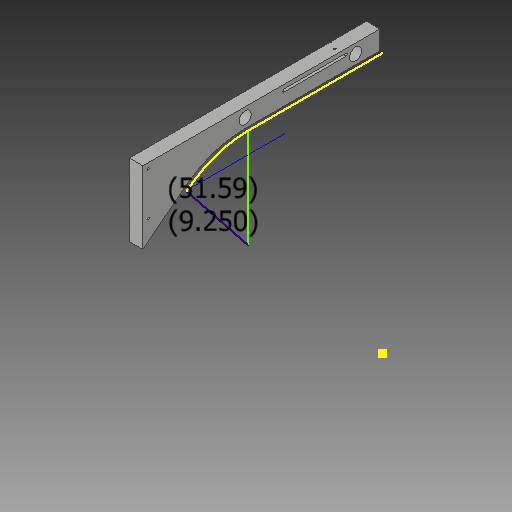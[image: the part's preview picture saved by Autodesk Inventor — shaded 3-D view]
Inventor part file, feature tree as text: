
AUTODESK INVENTOR PART (.ipt)
format: ipt  version: 2018 (Build 220112000, 112)  size: 167,936 bytes
history: native  units: in
note: dims shown in document units (in); Inventor stores cm internally (conversion verified against a paired STEP export)
features: direct_edit x4, move_body x4, other x1, sketch x1
ambient origin geometry x8: Origin, YZ Plane, XZ Plane, XY Plane, X Axis, Y Axis, Z Axis, Center Point
bodies: Solid1 (feature_tree)
feature tree (10):
  other  "RIGHT Bottom Part 1"
  direct_edit  "Direct Edit1"
  sketch  "Sketch2"  dims[d0=0.0in d1=0.0in d2=0.25in d5=9.25in d6=0.3545in d7=0.0in d8=0.0in d9=-0.125in d10=0.0in d11=0.0in d12=-0.375in d13=0.0in d14=0.0in d15=0.25in]
  direct_edit  "Direct Edit2"
  direct_edit  "Direct Edit3"
  direct_edit  "Direct Edit4"
  move_body  "Move1"
  move_body  "Move2"
  move_body  "Move3"
  move_body  "Move4"
